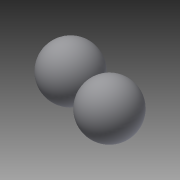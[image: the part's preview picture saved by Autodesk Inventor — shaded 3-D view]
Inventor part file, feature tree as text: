
AUTODESK INVENTOR PART (.ipt)
format: ipt  version: 2015 (Build 190159000, 159)  size: 123,392 bytes
history: native  units: in
note: dims shown in document units (in); Inventor stores cm internally (conversion verified against a paired STEP export)
features: revolve x2, sketch x2, plane x1
ambient origin geometry x8: Origin, YZ Plane, XZ Plane, XY Plane, X Axis, Y Axis, Z Axis, Center Point
bodies: Solid1 (feature_tree)
feature tree (5):
  revolve  "Revolution1"  Angle=90.0deg
  plane  "Work Plane1"
  revolve  "Revolution2"  [1 undecoded]
  sketch  "Sketch1"  dims[d0=0.4in d1=90.0deg]
  sketch  "Sketch2"  dims[d2=-0.1in d3=0.4in d4=90.0deg]
note: 1 required parameter value undecoded (feature->parameter linkage not recoverable at this tier; creation-order binding heuristic only, values carry confidence <= 0.55)
